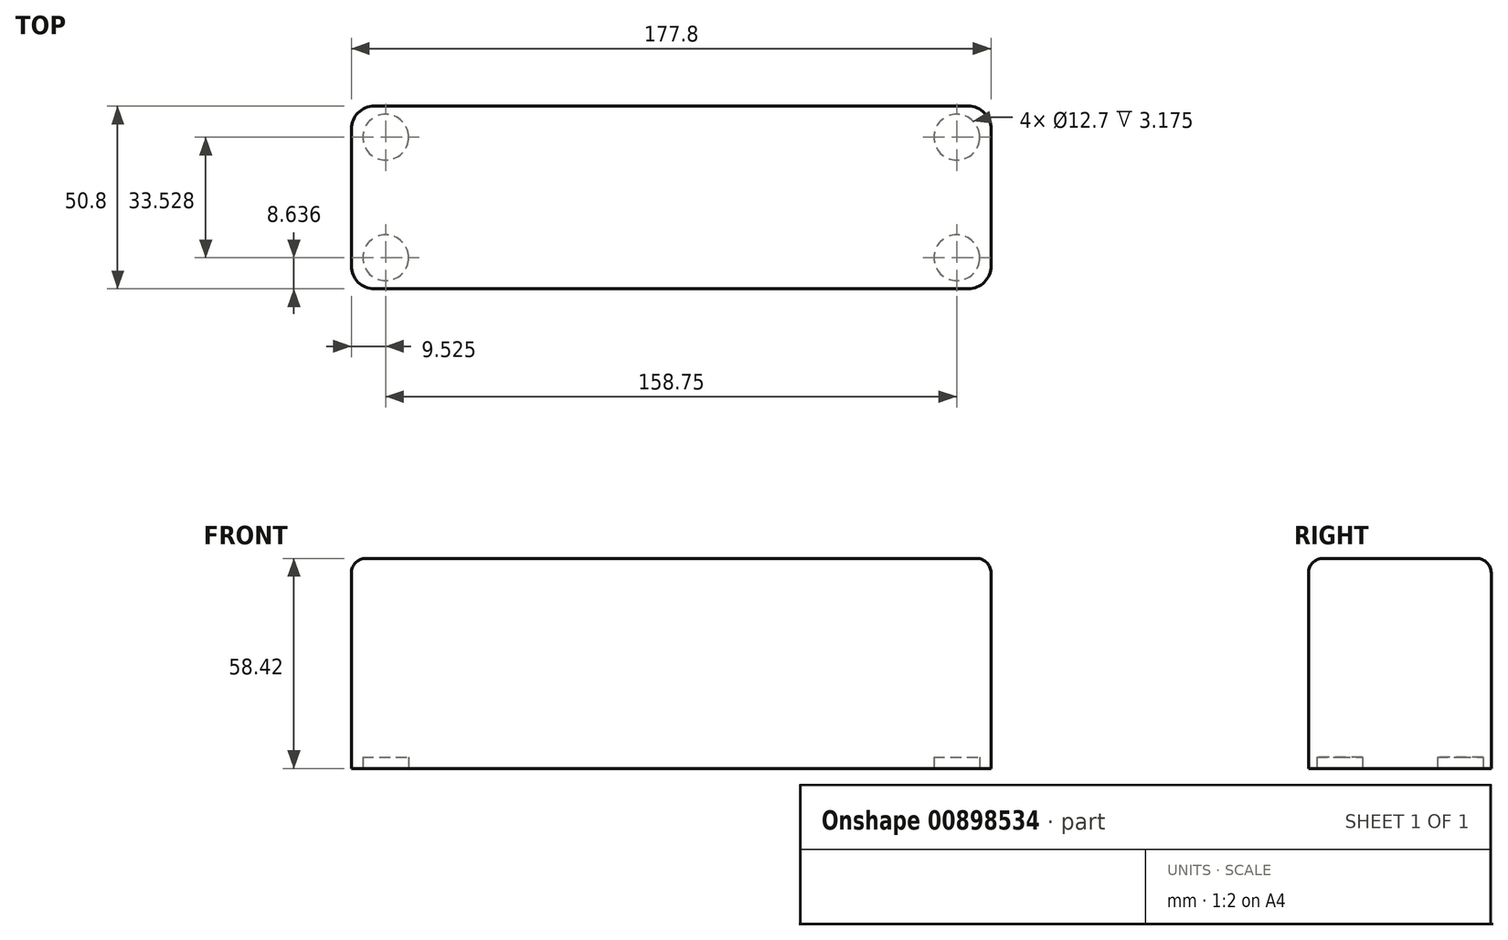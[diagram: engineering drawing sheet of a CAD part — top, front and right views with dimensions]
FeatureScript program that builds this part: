
annotation { "Feature Type Name" : "Feature", "Feature Type Description" : "" }
export const myFeature = defineFeature(function(context is Context, id is Id, definition is map)
    precondition{}
    {
        {
            var Q0;
            Q0=qCreatedBy(makeId("Top.planeOp"),FACE);
            var sketch = newSketch(context, id + "F0", { "sketchPlane" : qUnion([Q0])});
            skLineSegment(sketch, "E0.bottom", {"start": v(-88.9, 25.4) * mm, "end": v(88.9, 25.4) * mm});
            skLineSegment(sketch, "E0.top", {"start": v(-88.9, -25.4) * mm, "end": v(88.9, -25.4) * mm});
            skLineSegment(sketch, "E0.left", {"start": v(-88.9, 25.4) * mm, "end": v(-88.9, -25.4) * mm});
            skLineSegment(sketch, "E0.right", {"start": v(88.9, 25.4) * mm, "end": v(88.9, -25.4) * mm});
            skSolve(sketch);
        }
        {
            var Q0;
            Q0=makeQuery(id+"F0.imprint","IMPRINT",FACE,{"disambiguationData":[TD([[makeQuery(id+"F0.imprint","IMPRINT",EDGE,{"derivedFrom":sQuery(id+"F0.wireOp",EDGE,"E0.bottom")}),-1.0]])]});
            extrude(context, id + "F1", {"entities" : qUnion([Q0]), "depth" : 58.42 * mm, "offsetDistance" : 25.4 * mm});
        }
        {
            var Q0;
            Q0=makeQuery(id+"F1.opExtrude","SWEPT_EDGE",EDGE,{"disambiguationData":[OSD([sQuery(id+"F0.wireOp",EDGE,"E0.bottom"),sQuery(id+"F0.wireOp",EDGE,"E0.left")])]});
            var Q1;
            Q1=makeQuery(id+"F1.opExtrude","SWEPT_EDGE",EDGE,{"disambiguationData":[OSD([sQuery(id+"F0.wireOp",EDGE,"E0.bottom"),sQuery(id+"F0.wireOp",EDGE,"E0.right")])]});
            var Q2;
            Q2=makeQuery(id+"F1.opExtrude","SWEPT_EDGE",EDGE,{"disambiguationData":[OSD([sQuery(id+"F0.wireOp",EDGE,"E0.top"),sQuery(id+"F0.wireOp",EDGE,"E0.right")])]});
            var Q3;
            Q3=makeQuery(id+"F1.opExtrude","SWEPT_EDGE",EDGE,{"disambiguationData":[OSD([sQuery(id+"F0.wireOp",EDGE,"E0.top"),sQuery(id+"F0.wireOp",EDGE,"E0.left")])]});
            fillet(context, id + "F2", {"entities" : qUnion([Q0, Q1, Q2, Q3]), "radius" : 6.35 * mm, "tangentPropagation" : true, "allowEdgeOverflow" : false});
        }
        {
            var Q0;
            Q0=makeQuery(id+"F1.opExtrude","CAP_FACE",FACE,{"disambiguationData":[OSD([sQuery(id+"F0.wireOp",EDGE,"E0.bottom"),sQuery(id+"F0.wireOp",EDGE,"E0.top"),sQuery(id+"F0.wireOp",EDGE,"E0.left"),sQuery(id+"F0.wireOp",EDGE,"E0.right")])],"isStart":true});
            var sketch = newSketch(context, id + "F3", { "sketchPlane" : qUnion([Q0])});
            skCircle(sketch, "E1", {"center": v(79.38, 16.76) * mm, "radius": 6.35 * mm});
            skCircle(sketch, "E2.MirrorC", {"center": v(79.38, -16.76) * mm, "radius": 6.35 * mm});
            skCircle(sketch, "E3.MirrorC", {"center": v(-79.38, 16.76) * mm, "radius": 6.35 * mm});
            skCircle(sketch, "E4.MirrorC", {"center": v(-79.38, -16.76) * mm, "radius": 6.35 * mm});
            skSolve(sketch);
        }
        {
            var Q0;
            Q0=qSketchRegion(id+"F3",true);
            extrude(context, id + "F4", {"entities" : qUnion([Q0]), "operationType" : NewBodyOperationType.REMOVE, "oppositeDirection" : true, "depth" : 3.17 * mm, "offsetDistance" : 25.4 * mm});
        }
        {
            var Q0;
            Q0=makeQuery(id+"F1.opExtrude","CAP_FACE",FACE,{"disambiguationData":[OSD([sQuery(id+"F0.wireOp",EDGE,"E0.bottom"),sQuery(id+"F0.wireOp",EDGE,"E0.top"),sQuery(id+"F0.wireOp",EDGE,"E0.left"),sQuery(id+"F0.wireOp",EDGE,"E0.right")])],"isStart":true});
            var sketch = newSketch(context, id + "F5", { "sketchPlane" : qUnion([Q0])});
            skLineSegment(sketch, "E5", {"start": v(-79.38, -42.16) * mm, "end": v(-79.38, 42.16) * mm, "construction": true});
            skPoint(sketch, "E6", {"position": v(79.38, 16.76) * mm});
            skPoint(sketch, "E7", {"position": v(79.38, -16.76) * mm});
            skPoint(sketch, "E8", {"position": v(-79.38, -16.76) * mm});
            skPoint(sketch, "E9", {"position": v(-79.38, 16.76) * mm});
            skLineSegment(sketch, "E10", {"start": v(104.78, -16.76) * mm, "end": v(-104.78, -16.76) * mm, "construction": true});
            skLineSegment(sketch, "E11.MirrorCS", {"start": v(79.38, -42.16) * mm, "end": v(79.38, 42.16) * mm, "construction": true});
            skLineSegment(sketch, "E12.MirrorCS", {"start": v(104.78, 16.76) * mm, "end": v(-104.78, 16.76) * mm, "construction": true});
            skSolve(sketch);
        }
        {
            var Q0;
            {var subQ0=sQuery(id+"F0.wireOp",EDGE,"E0.right");var subQ1=sQuery(id+"F0.wireOp",EDGE,"E0.bottom");Q0=makeQuery(id+"F2.opFillet","BLEND_EDGE",EDGE,{"blendedFrom":[makeQuery(id+"F1.opExtrude","SWEPT_EDGE",EDGE,{"disambiguationData":[OSD([subQ1,subQ0])]}),makeQuery(id+"F1.opExtrude","CAP_FACE",FACE,{"disambiguationData":[OSD([subQ1,sQuery(id+"F0.wireOp",EDGE,"E0.top"),sQuery(id+"F0.wireOp",EDGE,"E0.left"),subQ0])],"isStart":false})],"blendedInto":[makeQuery(id+"F1.opExtrude","CAP_FACE",FACE,{"disambiguationData":[OSD([subQ1,sQuery(id+"F0.wireOp",EDGE,"E0.top"),sQuery(id+"F0.wireOp",EDGE,"E0.left"),subQ0])],"isStart":false})]});}
            var Q1;
            Q1=makeQuery(id+"F1.opExtrude","CAP_EDGE",EDGE,{"disambiguationData":[OSD([sQuery(id+"F0.wireOp",EDGE,"E0.right")])],"isStart":false});
            var Q2;
            {var subQ0=sQuery(id+"F0.wireOp",EDGE,"E0.right");var subQ1=sQuery(id+"F0.wireOp",EDGE,"E0.top");Q2=makeQuery(id+"F2.opFillet","BLEND_EDGE",EDGE,{"blendedFrom":[makeQuery(id+"F1.opExtrude","SWEPT_EDGE",EDGE,{"disambiguationData":[OSD([subQ1,subQ0])]}),makeQuery(id+"F1.opExtrude","CAP_FACE",FACE,{"disambiguationData":[OSD([sQuery(id+"F0.wireOp",EDGE,"E0.bottom"),subQ1,sQuery(id+"F0.wireOp",EDGE,"E0.left"),subQ0])],"isStart":false})],"blendedInto":[makeQuery(id+"F1.opExtrude","CAP_FACE",FACE,{"disambiguationData":[OSD([sQuery(id+"F0.wireOp",EDGE,"E0.bottom"),subQ1,sQuery(id+"F0.wireOp",EDGE,"E0.left"),subQ0])],"isStart":false})]});}
            var Q3;
            Q3=makeQuery(id+"F1.opExtrude","CAP_EDGE",EDGE,{"disambiguationData":[OSD([sQuery(id+"F0.wireOp",EDGE,"E0.top")])],"isStart":false});
            var Q4;
            Q4=makeQuery(id+"F1.opExtrude","CAP_EDGE",EDGE,{"disambiguationData":[OSD([sQuery(id+"F0.wireOp",EDGE,"E0.bottom")])],"isStart":false});
            var Q5;
            Q5=makeQuery(id+"F1.opExtrude","CAP_EDGE",EDGE,{"disambiguationData":[OSD([sQuery(id+"F0.wireOp",EDGE,"E0.left")])],"isStart":false});
            var Q6;
            {var subQ0=sQuery(id+"F0.wireOp",EDGE,"E0.left");var subQ1=sQuery(id+"F0.wireOp",EDGE,"E0.bottom");Q6=makeQuery(id+"F2.opFillet","BLEND_EDGE",EDGE,{"blendedFrom":[makeQuery(id+"F1.opExtrude","SWEPT_EDGE",EDGE,{"disambiguationData":[OSD([subQ1,subQ0])]}),makeQuery(id+"F1.opExtrude","CAP_FACE",FACE,{"disambiguationData":[OSD([subQ1,sQuery(id+"F0.wireOp",EDGE,"E0.top"),subQ0,sQuery(id+"F0.wireOp",EDGE,"E0.right")])],"isStart":false})],"blendedInto":[makeQuery(id+"F1.opExtrude","CAP_FACE",FACE,{"disambiguationData":[OSD([subQ1,sQuery(id+"F0.wireOp",EDGE,"E0.top"),subQ0,sQuery(id+"F0.wireOp",EDGE,"E0.right")])],"isStart":false})]});}
            var Q7;
            {var subQ0=sQuery(id+"F0.wireOp",EDGE,"E0.left");var subQ1=sQuery(id+"F0.wireOp",EDGE,"E0.top");Q7=makeQuery(id+"F2.opFillet","BLEND_EDGE",EDGE,{"blendedFrom":[makeQuery(id+"F1.opExtrude","SWEPT_EDGE",EDGE,{"disambiguationData":[OSD([subQ1,subQ0])]}),makeQuery(id+"F1.opExtrude","CAP_FACE",FACE,{"disambiguationData":[OSD([sQuery(id+"F0.wireOp",EDGE,"E0.bottom"),subQ1,subQ0,sQuery(id+"F0.wireOp",EDGE,"E0.right")])],"isStart":false})],"blendedInto":[makeQuery(id+"F1.opExtrude","CAP_FACE",FACE,{"disambiguationData":[OSD([sQuery(id+"F0.wireOp",EDGE,"E0.bottom"),subQ1,subQ0,sQuery(id+"F0.wireOp",EDGE,"E0.right")])],"isStart":false})]});}
            fillet(context, id + "F6", {"entities" : qUnion([Q0, Q1, Q2, Q3, Q4, Q5, Q6, Q7]), "radius" : 4 * mm, "allowEdgeOverflow" : false});
        }
    });
